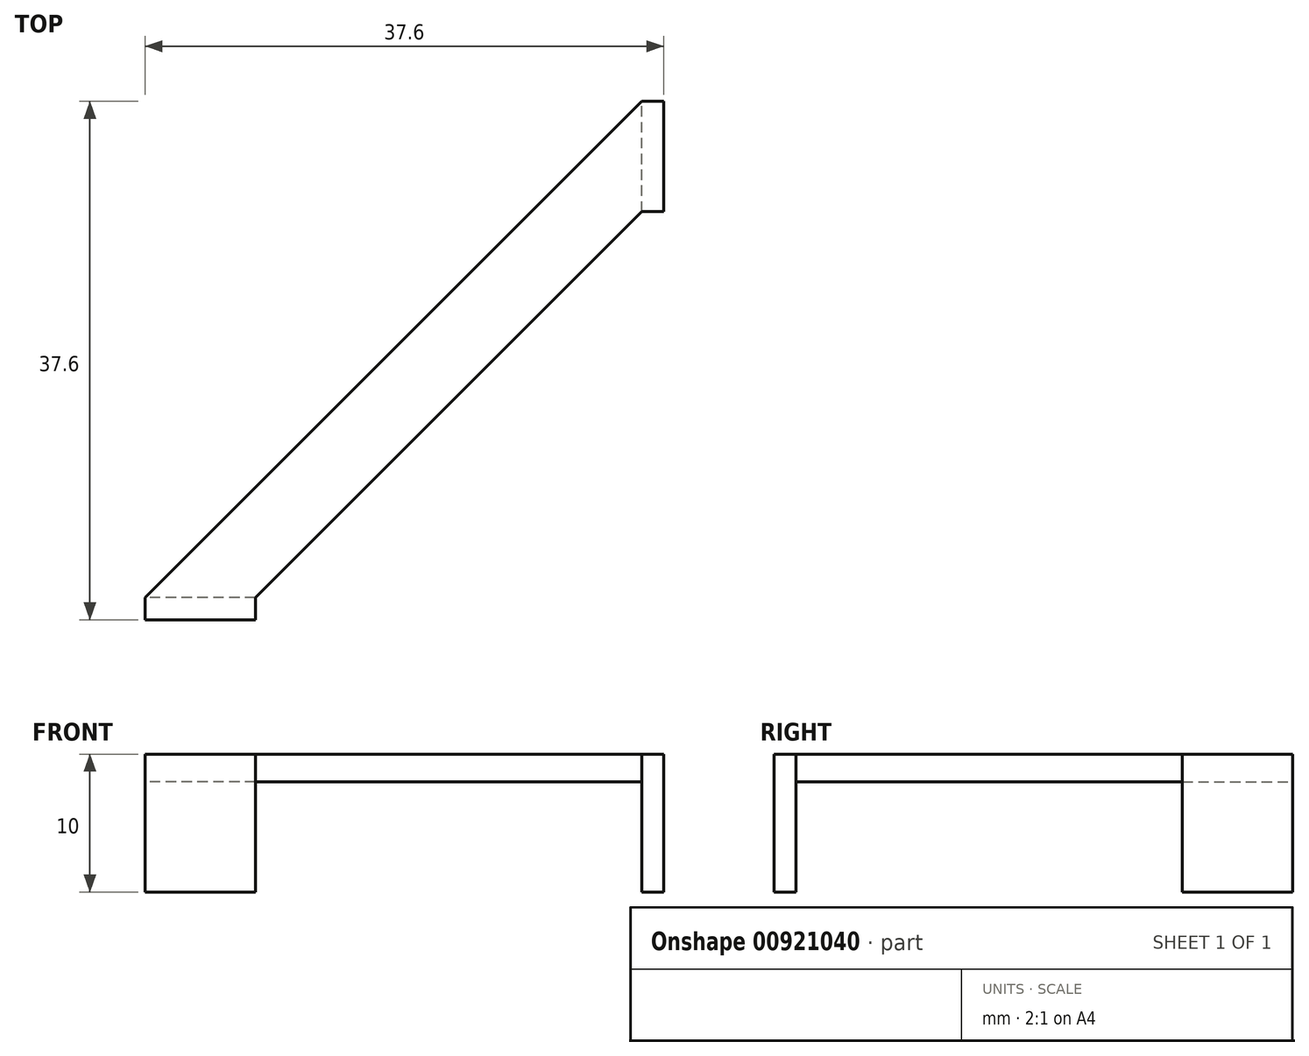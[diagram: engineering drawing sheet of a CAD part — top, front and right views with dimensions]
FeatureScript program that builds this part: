
annotation { "Feature Type Name" : "Feature", "Feature Type Description" : "" }
export const myFeature = defineFeature(function(context is Context, id is Id, definition is map)
    precondition{}
    {
        {
            var Q0;
            Q0=qCreatedBy(makeId("Top.planeOp"),FACE);
            var sketch = newSketch(context, id + "F0", { "sketchPlane" : qUnion([Q0])});
            skLineSegment(sketch, "E0", {"start": v(0, 0) * mm, "end": v(-28, 0) * mm, "construction": true});
            skLineSegment(sketch, "E1", {"start": v(-28, 0) * mm, "end": v(-36, 0) * mm});
            skLineSegment(sketch, "E2", {"start": v(0, 0) * mm, "end": v(0, 28) * mm, "construction": true});
            skLineSegment(sketch, "E3", {"start": v(0, 28) * mm, "end": v(-28, 0) * mm});
            skLineSegment(sketch, "E4", {"start": v(0, 28) * mm, "end": v(0, 36) * mm});
            skLineSegment(sketch, "E5", {"start": v(0, 36) * mm, "end": v(-36, 0) * mm});
            skLineSegment(sketch, "E6", {"start": v(-28, 0) * mm, "end": v(-28, -1.6) * mm});
            skLineSegment(sketch, "E7", {"start": v(-28, -1.6) * mm, "end": v(-36, -1.6) * mm});
            skLineSegment(sketch, "E8", {"start": v(-36, -1.6) * mm, "end": v(-36, 0) * mm});
            skLineSegment(sketch, "E9", {"start": v(0, 28) * mm, "end": v(1.6, 28) * mm});
            skLineSegment(sketch, "E10", {"start": v(1.6, 28) * mm, "end": v(1.6, 36) * mm});
            skLineSegment(sketch, "E11", {"start": v(1.6, 36) * mm, "end": v(0, 36) * mm});
            skSolve(sketch);
        }
        {
            var Q0;
            Q0 = qSketchRegion(id + "F0", true);
            extrude(context, id + "F1", {"entities" : qUnion([Q0]), "depth" : 2 * mm, "offsetDistance" : 25 * mm});
        }
        {
            var Q0;
            Q0=makeQuery(id+"F0.imprint","IMPRINT",FACE,{"disambiguationData":[TD([[makeQuery(id+"F0.imprint","IMPRINT",EDGE,{"derivedFrom":sQuery(id+"F0.wireOp",EDGE,"E4")}),-1.0]])]});
            var Q1;
            Q1=makeQuery(id+"F0.imprint","IMPRINT",FACE,{"disambiguationData":[TD([[makeQuery(id+"F0.imprint","IMPRINT",EDGE,{"derivedFrom":sQuery(id+"F0.wireOp",EDGE,"E1")}),1.0]])]});
            extrude(context, id + "F2", {"entities" : qUnion([Q0, Q1]), "operationType" : NewBodyOperationType.ADD, "oppositeDirection" : true, "depth" : 8 * mm, "offsetDistance" : 25 * mm});
        }
    });
